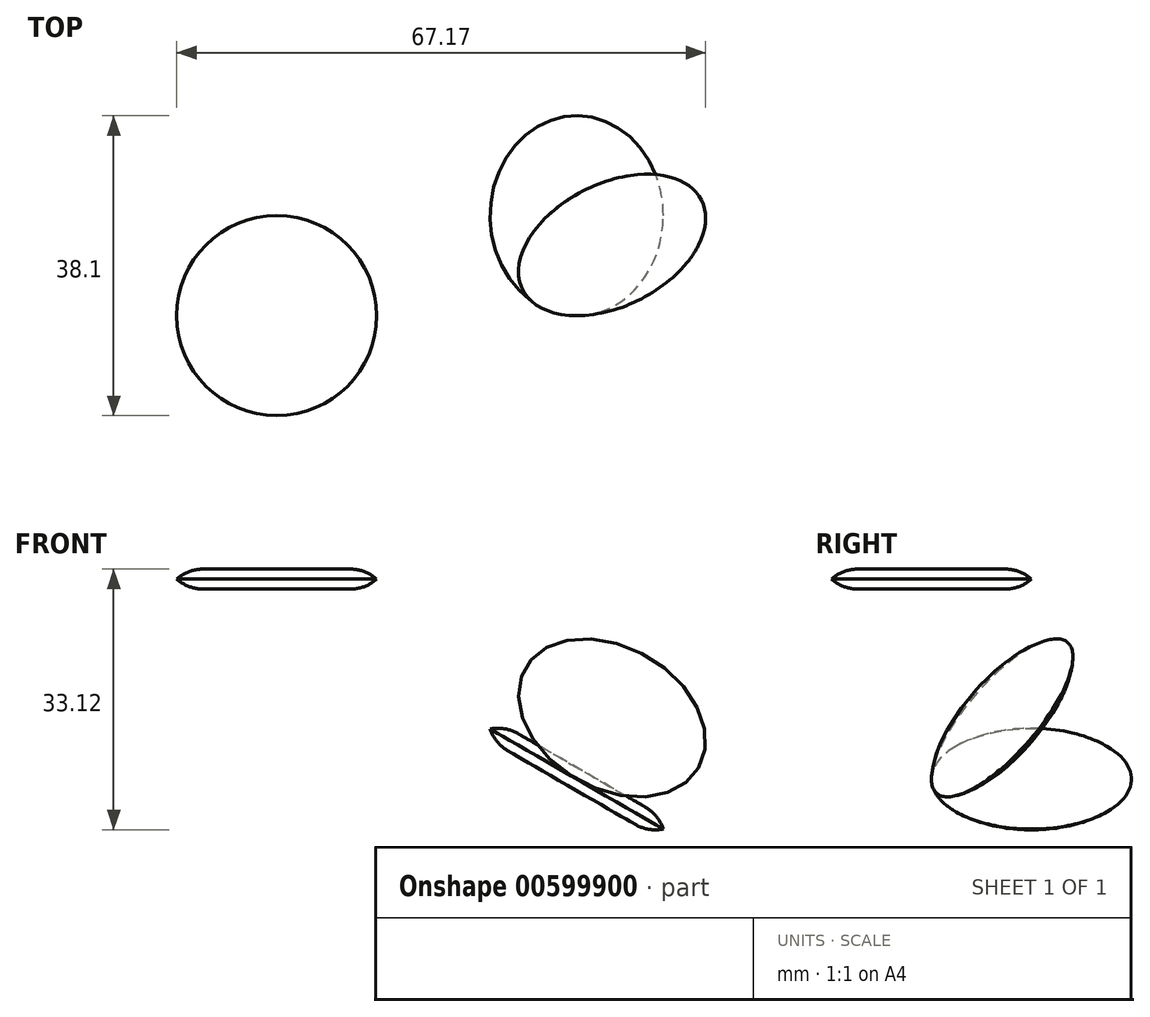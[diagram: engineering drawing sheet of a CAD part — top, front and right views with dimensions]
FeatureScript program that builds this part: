
annotation { "Feature Type Name" : "Feature", "Feature Type Description" : "" }
export const myFeature = defineFeature(function(context is Context, id is Id, definition is map)
    precondition{}
    {
        {
            var Q0;
            Q0=qCreatedBy(makeId("Top.planeOp"),FACE);
            var sketch = newSketch(context, id + "F0", { "sketchPlane" : qUnion([Q0])});
            skCircle(sketch, "E0", {"center": v(0, 0) * mm, "radius": 12.7 * mm});
            skSolve(sketch);
        }
        {
            var Q0;
            Q0=qSketchRegion(id+"F0",true);
            extrude(context, id + "F1", {"entities" : qUnion([Q0]), "endBound" : BoundingType.SYMMETRIC, "depth" : 2.54 * mm, "offsetDistance" : 25.4 * mm});
        }
        {
            var Q0;
            Q0=makeQuery(id+"F1.opExtrude","CAP_EDGE",EDGE,{"disambiguationData":[OSD([sQuery(id+"F0.wireOp",EDGE,"E0")])],"isStart":true});
            var Q1;
            Q1=makeQuery(id+"F1.opExtrude","CAP_EDGE",EDGE,{"disambiguationData":[OSD([sQuery(id+"F0.wireOp",EDGE,"E0")])],"isStart":false});
            chamfer(context, id + "F2", {"entities" : qUnion([Q0, Q1]), "width" : 1.27 * mm, "tangentPropagation" : true});
        }
        {
            var Q0;
            {var subQ0=sQuery(id+"F0.wireOp",EDGE,"E0");Q0=makeQuery(id+"F2.opChamfer","BLEND_EDGE",EDGE,{"blendedFrom":[makeQuery(id+"F1.opExtrude","CAP_EDGE",EDGE,{"disambiguationData":[OSD([subQ0])],"isStart":false}),makeQuery(id+"F1.opExtrude","CAP_FACE",FACE,{"disambiguationData":[OSD([subQ0])],"isStart":false})],"blendedInto":[makeQuery(id+"F1.opExtrude","CAP_FACE",FACE,{"disambiguationData":[OSD([subQ0])],"isStart":false})]});}
            fillet(context, id + "F3", {"entities" : qUnion([Q0]), "radius" : 5.08 * mm, "tangentPropagation" : true, "allowEdgeOverflow" : false});
        }
        {
            var Q0;
            {var subQ0=sQuery(id+"F0.wireOp",EDGE,"E0");Q0=makeQuery(id+"F2.opChamfer","BLEND_EDGE",EDGE,{"blendedFrom":[makeQuery(id+"F1.opExtrude","CAP_EDGE",EDGE,{"disambiguationData":[OSD([subQ0])],"isStart":true}),makeQuery(id+"F1.opExtrude","CAP_FACE",FACE,{"disambiguationData":[OSD([subQ0])],"isStart":true})],"blendedInto":[makeQuery(id+"F1.opExtrude","CAP_FACE",FACE,{"disambiguationData":[OSD([subQ0])],"isStart":true})]});}
            fillet(context, id + "F4", {"entities" : qUnion([Q0]), "radius" : 5.08 * mm, "tangentPropagation" : true, "allowEdgeOverflow" : false});
        }
        {
            var Q0;
            Q0=makeQuery(id+"F1.opExtrude","SWEPT_BODY",BODY,{"disambiguationData":[OSD([sQuery(id+"F0.wireOp",EDGE,"E0")])]});
            transform(context, id + "F5", {"entities" : qUnion([Q0]), "transformType" : TransformType.TRANSLATION_3D, "dx" : 38.1 * mm, "dy" : 12.7 * mm, "dz" : -25.4 * mm, "makeCopy" : true});
        }
        {
            var Q0;
            Q0=makeQuery(id+"F5.opPattern","COPY",FACE,{"derivedFrom":makeQuery(id+"F1.opExtrude","CAP_FACE",FACE,{"disambiguationData":[OSD([sQuery(id+"F0.wireOp",EDGE,"E0")])],"isStart":false}),"instanceName":"1"});
            cPlane(context, id + "F6", {"entities" : qUnion([Q0]), "cplaneType" : CPlaneType.OFFSET, "offset" : 1.27 * mm, "oppositeDirection" : true, "width" : 152.4 * mm, "height" : 152.4 * mm});
        }
        {
            var Q0;
            Q0=qCreatedBy(id+"F6.planeOp",FACE);
            var sketch = newSketch(context, id + "F7", { "sketchPlane" : qUnion([Q0])});
            skCircle(sketch, "E1.0", {"center": v(38.1, 12.7) * mm, "radius": 9.34 * mm});
            skLineSegment(sketch, "E2", {"start": v(38.1, 12.7) * mm, "end": v(38.1, 37.81) * mm});
            skLineSegment(sketch, "E3", {"start": v(38.1, 37.81) * mm, "end": v(38.1, -2.87) * mm});
            skSolve(sketch);
        }
        {
            var Q0;
            Q0=makeQuery(id+"F5.opPattern","COPY",BODY,{"derivedFrom":makeQuery(id+"F1.opExtrude","SWEPT_BODY",BODY,{"disambiguationData":[OSD([sQuery(id+"F0.wireOp",EDGE,"E0")])]}),"instanceName":"1"});
            var Q1;
            Q1=sQuery(id+"F7.wireOp",EDGE,"E3");
            transform(context, id + "F8", {"entities" : qUnion([Q0]), "transformType" : TransformType.ROTATION, "transformAxis" : qUnion([Q1]), "angle" : 30 * degree, "oppositeDirection" : true, "makeCopy" : false});
        }
        {
            var Q0;
            Q0=makeQuery(id+"F5.opPattern","COPY",FACE,{"derivedFrom":makeQuery(id+"F1.opExtrude","CAP_FACE",FACE,{"disambiguationData":[OSD([sQuery(id+"F0.wireOp",EDGE,"E0")])],"isStart":false}),"instanceName":"1"});
            cPlane(context, id + "F9", {"entities" : qUnion([Q0]), "cplaneType" : CPlaneType.OFFSET, "offset" : 1.27 * mm, "oppositeDirection" : true, "width" : 152.4 * mm, "height" : 152.4 * mm});
        }
        {
            var Q0;
            Q0=qCreatedBy(id+"F9.planeOp",FACE);
            var sketch = newSketch(context, id + "F10", { "sketchPlane" : qUnion([Q0])});
            skCircle(sketch, "E4.0", {"center": v(45.7, 12.7) * mm, "radius": 12.7 * mm});
            skLineSegment(sketch, "E5", {"start": v(45.7, 0) * mm, "end": v(60.1, 0) * mm});
            skLineSegment(sketch, "E6", {"start": v(60.1, 0) * mm, "end": v(20.4, 0) * mm});
            skSolve(sketch);
        }
        {
            var Q0;
            Q0=makeQuery(id+"F5.opPattern","COPY",BODY,{"derivedFrom":makeQuery(id+"F1.opExtrude","SWEPT_BODY",BODY,{"disambiguationData":[OSD([sQuery(id+"F0.wireOp",EDGE,"E0")])]}),"instanceName":"1"});
            var Q1;
            Q1=sQuery(id+"F10.wireOp",EDGE,"E6");
            transform(context, id + "F11", {"entities" : qUnion([Q0]), "transformType" : TransformType.ROTATION, "transformAxis" : qUnion([Q1]), "angle" : 45 * degree, "oppositeDirection" : true, "makeCopy" : true});
        }
    });
